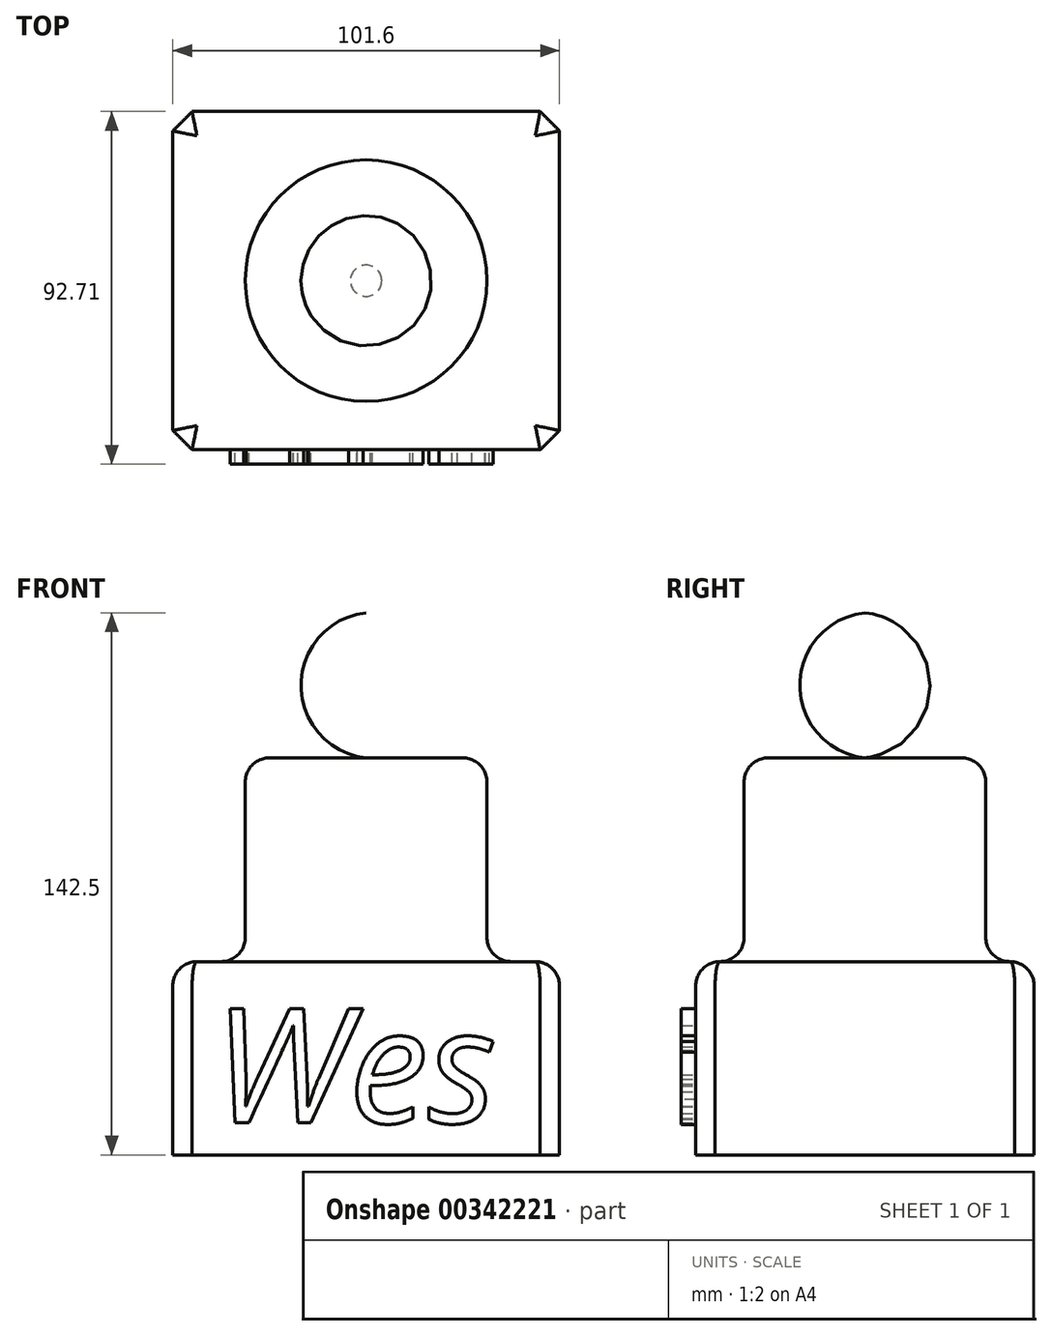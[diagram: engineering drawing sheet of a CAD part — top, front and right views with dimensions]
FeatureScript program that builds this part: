
annotation { "Feature Type Name" : "Feature", "Feature Type Description" : "" }
export const myFeature = defineFeature(function(context is Context, id is Id, definition is map)
    precondition{}
    {
        {
            var Q0;
            Q0=qCreatedBy(makeId("Front.planeOp"),FACE);
            var sketch = newSketch(context, id + "F0", { "sketchPlane" : qUnion([Q0])});
            skLineSegment(sketch, "E0.bottom", {"start": v(-50.8, -21.8) * mm, "end": v(50.8, -21.8) * mm});
            skLineSegment(sketch, "E0.top", {"start": v(-50.8, -72.6) * mm, "end": v(50.8, -72.6) * mm});
            skLineSegment(sketch, "E0.left", {"start": v(-50.8, -21.8) * mm, "end": v(-50.8, -72.6) * mm});
            skLineSegment(sketch, "E0.right", {"start": v(50.8, -21.8) * mm, "end": v(50.8, -72.6) * mm});
            skPoint(sketch, "E0.middle", {"position": v(0, -47.2) * mm});
            skText(sketch, "E1", { "text": "Wes", "fontName": "AllertaStencil-Regular.ttf"});
            const initialGuessF0  = {"E1": [-0.19955, -0.05196, 1, 0, 0.03047]};
            skSetInitialGuess(sketch, initialGuessF0);
            skSolve(sketch);
        }
        {
            var Q0;
            Q0=qCreatedBy(makeId("Front.planeOp"),FACE);
            var sketch = newSketch(context, id + "F1", { "sketchPlane" : qUnion([Q0])});
            skLineSegment(sketch, "E2.bottom", {"start": v(-31.75, 31.75) * mm, "end": v(31.75, 31.75) * mm});
            skLineSegment(sketch, "E2.top", {"start": v(-31.75, -31.75) * mm, "end": v(31.75, -31.75) * mm});
            skLineSegment(sketch, "E2.left", {"start": v(-31.75, 31.75) * mm, "end": v(-31.75, -31.75) * mm});
            skLineSegment(sketch, "E2.right", {"start": v(31.75, 31.75) * mm, "end": v(31.75, -31.75) * mm});
            skPoint(sketch, "E2.middle", {"position": v(0, 0) * mm});
            skArc(sketch, "E3", {"start": v(0, 69.9) * mm, "mid": v(-21.24, 50.82) * mm, "end": v(0, 31.75) * mm});
            skPoint(sketch, "E3.startSnap0", {"position": v(0, 31.75) * mm});
            skLineSegment(sketch, "E4", {"start": v(0, 69.9) * mm, "end": v(0, -31.75) * mm});
            skSolve(sketch);
        }
        {
            var Q0;
            Q0=makeQuery(id+"F0.imprint","IMPRINT",FACE,{"disambiguationData":[TD([[makeQuery(id+"F0.imprint","IMPRINT",EDGE,{"derivedFrom":sQuery(id+"F0.wireOp",EDGE,"E0.bottom")}),-1.0]])]});
            extrude(context, id + "F2", {"entities" : qUnion([Q0]), "endBound" : BoundingType.SYMMETRIC, "depth" : 88.9 * mm});
        }
        {
            var Q0;
            {var subQ0=sQuery(id+"F1.wireOp",EDGE,"E4");var subQ1=sQuery(id+"F1.wireOp",EDGE,"E3");var subQ5=makeQuery(id+"F1.imprint","INTERSECT",VERTEX,{"derivedFrom":[subQ1,subQ0]});Q0=makeQuery(id+"F1.imprint","IMPRINT",FACE,{"disambiguationData":[TD([[makeQuery(id+"F1.imprint","IMPRINT",EDGE,{"disambiguationData":[TD([[subQ5,-1.0]])],"derivedFrom":subQ1}),1.0]])]});}
            var Q1;
            {var subQ5=sQuery(id+"F1.wireOp",EDGE,"E2.left");Q1=makeQuery(id+"F1.imprint","IMPRINT",FACE,{"disambiguationData":[TD([[makeQuery(id+"F1.imprint","IMPRINT",EDGE,{"derivedFrom":subQ5}),1.0]])]});}
            var Q2;
            Q2=sQuery(id+"F1.wireOp",EDGE,"E4");
            revolve(context, id + "F3", {"operationType" : NewBodyOperationType.ADD, "entities" : qUnion([Q0, Q1]), "axis" : qUnion([Q2]), "revolveType" : RevolveType.FULL});
        }
        {
            var Q0;
            Q0=makeQuery(id+"F3.opRevolve","SWEPT_EDGE",EDGE,{"disambiguationData":[OSD([sQuery(id+"F1.wireOp",EDGE,"E2.bottom"),sQuery(id+"F1.wireOp",EDGE,"E2.left")])]});
            var Q1;
            Q1=makeQuery(id+"F2.opExtrude","CAP_EDGE",EDGE,{"disambiguationData":[OSD([sQuery(id+"F0.wireOp",EDGE,"E0.bottom")])],"isStart":false});
            var Q2;
            Q2=makeQuery(id+"F2.opExtrude","SWEPT_EDGE",EDGE,{"disambiguationData":[OSD([sQuery(id+"F0.wireOp",EDGE,"E0.bottom"),sQuery(id+"F0.wireOp",EDGE,"E0.left")])]});
            var Q3;
            Q3=makeQuery(id+"F2.opExtrude","CAP_EDGE",EDGE,{"disambiguationData":[OSD([sQuery(id+"F0.wireOp",EDGE,"E0.bottom")])],"isStart":true});
            var Q4;
            Q4=makeQuery(id+"F2.opExtrude","SWEPT_EDGE",EDGE,{"disambiguationData":[OSD([sQuery(id+"F0.wireOp",EDGE,"E0.bottom"),sQuery(id+"F0.wireOp",EDGE,"E0.right")])]});
            var Q5;
            Q5=makeQuery(id+"F3.boolean.opBoolean","INTERSECT",EDGE,{"derivedFrom":[makeQuery(id+"F2.opExtrude","SWEPT_FACE",FACE,{"disambiguationData":[OSD([sQuery(id+"F0.wireOp",EDGE,"E0.bottom")])]}),makeQuery(id+"F3.opRevolve","SWEPT_FACE",FACE,{"disambiguationData":[OSD([sQuery(id+"F1.wireOp",EDGE,"E2.left")])]})]});
            fillet(context, id + "F4", {"entities" : qUnion([Q0, Q1, Q2, Q3, Q4, Q5]), "radius" : 6.35 * mm, "tangentPropagation" : true, "allowEdgeOverflow" : false});
        }
        {
            var Q0;
            Q0=makeQuery(id+"F2.opExtrude","CAP_EDGE",EDGE,{"disambiguationData":[OSD([sQuery(id+"F0.wireOp",EDGE,"E0.left")])],"isStart":false});
            var Q1;
            Q1=makeQuery(id+"F2.opExtrude","CAP_EDGE",EDGE,{"disambiguationData":[OSD([sQuery(id+"F0.wireOp",EDGE,"E0.right")])],"isStart":false});
            var Q2;
            Q2=makeQuery(id+"F2.opExtrude","CAP_EDGE",EDGE,{"disambiguationData":[OSD([sQuery(id+"F0.wireOp",EDGE,"E0.right")])],"isStart":true});
            var Q3;
            Q3=makeQuery(id+"F2.opExtrude","CAP_EDGE",EDGE,{"disambiguationData":[OSD([sQuery(id+"F0.wireOp",EDGE,"E0.left")])],"isStart":true});
            chamfer(context, id + "F5", {"entities" : qUnion([Q0, Q1, Q2, Q3]), "width" : 5.08 * mm, "tangentPropagation" : true});
        }
        {
            var Q0;
            Q0=makeQuery(id+"F2.opExtrude","CAP_FACE",FACE,{"disambiguationData":[OSD([sQuery(id+"F0.wireOp",EDGE,"E0.bottom"),sQuery(id+"F0.wireOp",EDGE,"E0.top"),sQuery(id+"F0.wireOp",EDGE,"E0.left"),sQuery(id+"F0.wireOp",EDGE,"E0.right")])],"isStart":false});
            var sketch = newSketch(context, id + "F6", { "sketchPlane" : qUnion([Q0])});
            skText(sketch, "E5", { "text": "Wes", "fontName": "OpenSans-Italic.ttf"});
            const initialGuessF6  = {"E5": [-0.04024, -0.0642, 1, 0, 0.03024]};
            skSetInitialGuess(sketch, initialGuessF6);
            skSolve(sketch);
        }
        {
            var Q0;
            Q0 = qSketchRegion(id + "F6", true);
            extrude(context, id + "F7", {"entities" : qUnion([Q0]), "operationType" : NewBodyOperationType.ADD, "depth" : 3.8 * mm});
        }
    });
